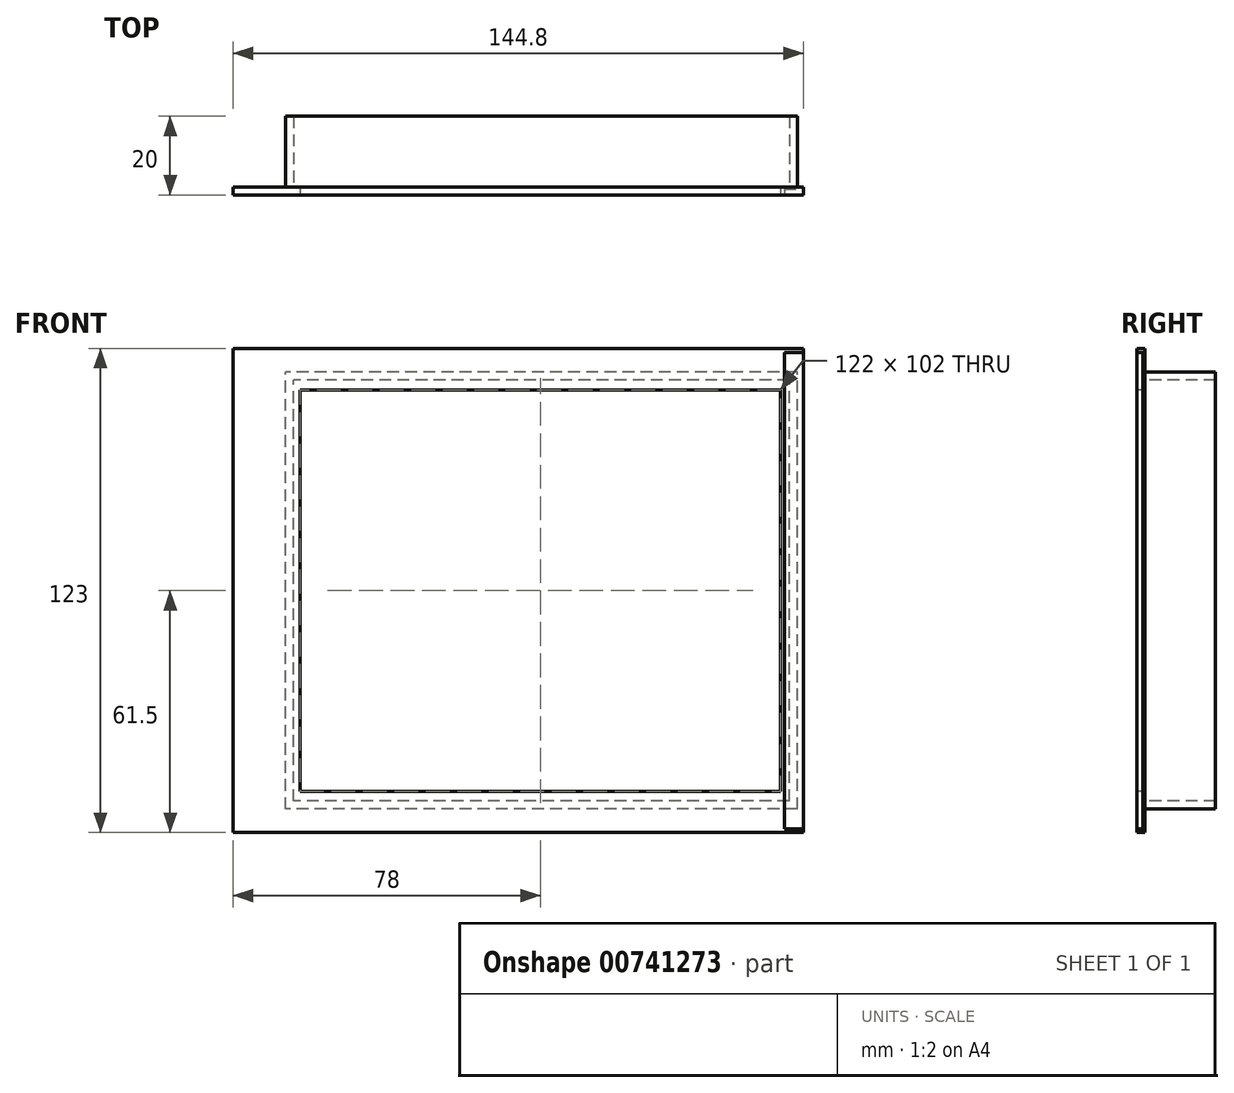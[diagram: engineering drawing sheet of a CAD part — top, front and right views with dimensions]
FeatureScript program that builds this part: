
annotation { "Feature Type Name" : "Feature", "Feature Type Description" : "" }
export const myFeature = defineFeature(function(context is Context, id is Id, definition is map)
    precondition{}
    {
        {
            var Q0;
            Q0=qCreatedBy(makeId("Front.planeOp"),FACE);
            var sketch = newSketch(context, id + "F0", { "sketchPlane" : qUnion([Q0])});
            skLineSegment(sketch, "E0.bottom", {"start": v(51.5, -39) * mm, "end": v(-51.5, -39) * mm, "construction": true});
            skLineSegment(sketch, "E0.top", {"start": v(51.5, 39) * mm, "end": v(-51.5, 39) * mm, "construction": true});
            skLineSegment(sketch, "E0.left", {"start": v(51.5, -39) * mm, "end": v(51.5, 39) * mm, "construction": true});
            skLineSegment(sketch, "E0.right", {"start": v(-51.5, -39) * mm, "end": v(-51.5, 39) * mm, "construction": true});
            skLineSegment(sketch, "E1.bottom", {"start": v(-61.3, 51) * mm, "end": v(60.7, 51) * mm});
            skLineSegment(sketch, "E1.top", {"start": v(-61.3, -51) * mm, "end": v(60.7, -51) * mm});
            skLineSegment(sketch, "E1.left", {"start": v(-61.3, 51) * mm, "end": v(-61.3, -51) * mm});
            skLineSegment(sketch, "E1.right", {"start": v(60.7, 51) * mm, "end": v(60.7, -51) * mm});
            skPoint(sketch, "E2.middle", {"position": v(0, 0) * mm});
            skLineSegment(sketch, "E3.bottom", {"start": v(66.5, -61.5) * mm, "end": v(-78.3, -61.5) * mm});
            skLineSegment(sketch, "E3.top", {"start": v(66.5, 61.5) * mm, "end": v(-78.3, 61.5) * mm});
            skLineSegment(sketch, "E3.left", {"start": v(66.5, -61.5) * mm, "end": v(66.5, 61.5) * mm});
            skLineSegment(sketch, "E3.right", {"start": v(-78.3, -61.5) * mm, "end": v(-78.3, 61.5) * mm});
            skPoint(sketch, "E3.middle", {"position": v(-5.9, 0) * mm});
            skLineSegment(sketch, "E4.bottom", {"start": v(65, -55.5) * mm, "end": v(-65, -55.5) * mm});
            skLineSegment(sketch, "E4.top", {"start": v(65, 55.5) * mm, "end": v(-65, 55.5) * mm});
            skLineSegment(sketch, "E4.left", {"start": v(65, -55.5) * mm, "end": v(65, 55.5) * mm});
            skLineSegment(sketch, "E4.right", {"start": v(-65, -55.5) * mm, "end": v(-65, 55.5) * mm});
            skLineSegment(sketch, "E5.0", {"start": v(63, 53.5) * mm, "end": v(-63, 53.5) * mm});
            skLineSegment(sketch, "E5.1", {"start": v(63, -53.5) * mm, "end": v(63, 53.5) * mm});
            skLineSegment(sketch, "E5.2", {"start": v(63, -53.5) * mm, "end": v(-63, -53.5) * mm});
            skLineSegment(sketch, "E5.3", {"start": v(-63, -53.5) * mm, "end": v(-63, 53.5) * mm});
            skLineSegment(sketch, "E6.bottom", {"start": v(66.5, 60.5) * mm, "end": v(61.7, 60.5) * mm});
            skLineSegment(sketch, "E6.right", {"start": v(61.7, 60.5) * mm, "end": v(61.7, -60.5) * mm});
            skLineSegment(sketch, "E7", {"start": v(61.7, -60.5) * mm, "end": v(66.5, -60.5) * mm});
            skLineSegment(sketch, "E8", {"start": v(66.5, -60.5) * mm, "end": v(66.5, 60.5) * mm});
            skSolve(sketch);
        }
        {
            var Q0;
            {var subQ8=sQuery(id+"F0.wireOp",EDGE,"E3.bottom");Q0=makeQuery(id+"F0.imprint","IMPRINT",FACE,{"disambiguationData":[TD([[makeQuery(id+"F0.imprint","IMPRINT",EDGE,{"derivedFrom":subQ8}),-1.0]])]});}
            var Q1;
            {var subQ7=sQuery(id+"F0.wireOp",EDGE,"E4.right");var subQ14=sQuery(id+"F0.wireOp",EDGE,"E4.left");Q1=qUnion([makeQuery(id+"F0.imprint","IMPRINT",FACE,{"disambiguationData":[TD([[makeQuery(id+"F0.imprint","IMPRINT",EDGE,{"derivedFrom":subQ14}),1.0]])]}),makeQuery(id+"F0.imprint","IMPRINT",FACE,{"disambiguationData":[TD([[makeQuery(id+"F0.imprint","IMPRINT",EDGE,{"derivedFrom":subQ7}),-1.0]])]})]);}
            var Q2;
            Q2=makeQuery(id+"F0.imprint","IMPRINT",FACE,{"disambiguationData":[TD([[makeQuery(id+"F0.imprint","IMPRINT",EDGE,{"derivedFrom":sQuery(id+"F0.wireOp",EDGE,"E1.bottom")}),1.0]])]});
            var Q3;
            {var subQ0=sQuery(id+"F0.wireOp",EDGE,"E4.left");Q3=makeQuery(id+"F0.imprint","IMPRINT",FACE,{"disambiguationData":[TD([[makeQuery(id+"F0.imprint","IMPRINT",EDGE,{"derivedFrom":subQ0}),-1.0]])]});}
            var Q4;
            {var subQ3=sQuery(id+"F0.wireOp",EDGE,"E5.1");Q4=makeQuery(id+"F0.imprint","IMPRINT",FACE,{"disambiguationData":[TD([[makeQuery(id+"F0.imprint","IMPRINT",EDGE,{"derivedFrom":subQ3}),1.0]])]});}
            extrude(context, id + "F1", {"entities" : qUnion([Q0, Q1, Q2, Q3, Q4]), "oppositeDirection" : true, "depth" : 2 * mm, "offsetDistance" : 25 * mm});
        }
        {
            var Q0;
            {var subQ7=sQuery(id+"F0.wireOp",EDGE,"E4.right");var subQ14=sQuery(id+"F0.wireOp",EDGE,"E4.left");Q0=qUnion([makeQuery(id+"F0.imprint","IMPRINT",FACE,{"disambiguationData":[TD([[makeQuery(id+"F0.imprint","IMPRINT",EDGE,{"derivedFrom":subQ14}),1.0]])]}),makeQuery(id+"F0.imprint","IMPRINT",FACE,{"disambiguationData":[TD([[makeQuery(id+"F0.imprint","IMPRINT",EDGE,{"derivedFrom":subQ7}),-1.0]])]})]);}
            extrude(context, id + "F2", {"entities" : qUnion([Q0]), "operationType" : NewBodyOperationType.ADD, "oppositeDirection" : true, "depth" : 20 * mm, "offsetDistance" : 25 * mm});
        }
        {
            var Q0;
            {var subQ0=sQuery(id+"F0.wireOp",EDGE,"E4.left");Q0=makeQuery(id+"F0.imprint","IMPRINT",FACE,{"disambiguationData":[TD([[makeQuery(id+"F0.imprint","IMPRINT",EDGE,{"derivedFrom":subQ0}),-1.0]])]});}
            var Q1;
            {var subQ3=sQuery(id+"F0.wireOp",EDGE,"E5.1");Q1=makeQuery(id+"F0.imprint","IMPRINT",FACE,{"disambiguationData":[TD([[makeQuery(id+"F0.imprint","IMPRINT",EDGE,{"derivedFrom":subQ3}),1.0]])]});}
            var Q2;
            {var subQ4=sQuery(id+"F0.wireOp",EDGE,"E4.left");Q2=makeQuery(id+"F0.imprint","IMPRINT",FACE,{"disambiguationData":[TD([[makeQuery(id+"F0.imprint","IMPRINT",EDGE,{"derivedFrom":subQ4}),1.0]])]});}
            extrude(context, id + "F3", {"entities" : qUnion([Q0, Q1, Q2]), "operationType" : NewBodyOperationType.REMOVE, "oppositeDirection" : true, "depth" : 1.5 * mm, "offsetDistance" : 25 * mm, "hasSecondDirection" : true, "secondDirectionOppositeDirection" : false, "secondDirectionDepth" : 2 * mm});
        }
    });
